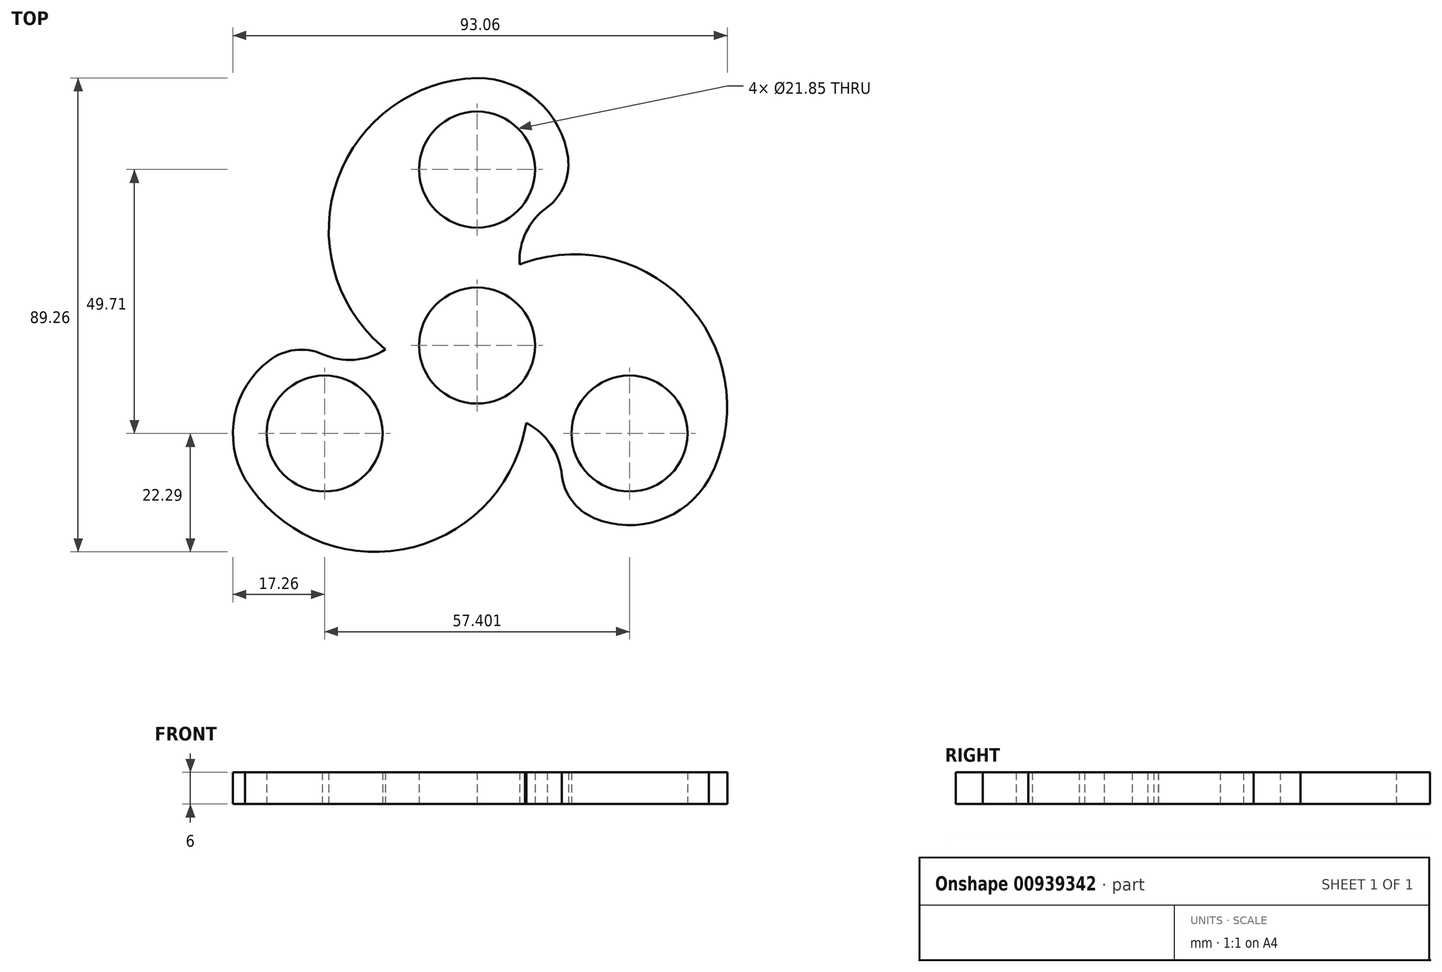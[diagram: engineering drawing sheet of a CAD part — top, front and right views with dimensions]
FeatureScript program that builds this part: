
annotation { "Feature Type Name" : "Feature", "Feature Type Description" : "" }
export const myFeature = defineFeature(function(context is Context, id is Id, definition is map)
    precondition{}
    {
        {
            var Q0;
            Q0=qCreatedBy(makeId("Top.planeOp"),FACE);
            var sketch = newSketch(context, id + "F0", { "sketchPlane" : qUnion([Q0])});
            skCircle(sketch, "E0", {"center": v(0, 0) * mm, "radius": 277.5 * mm});
            skCircle(sketch, "E1", {"center": v(0, 0) * mm, "radius": 266.7 * mm});
            skCircle(sketch, "E2", {"center": v(0, 0) * mm, "radius": 10.93 * mm});
            skCircle(sketch, "E3", {"center": v(0, 33.14) * mm, "radius": 10.93 * mm});
            skArc(sketch, "E4", {"start": v(17.13, 35.3) * mm, "mid": v(11.42, 46.09) * mm, "end": v(0, 50.4) * mm});
            skPoint(sketch, "E5.visualSharp", {"position": v(16.45, 27.92) * mm});
            skArc(sketch, "E5.filletArc", {"start": v(13.2, 26.04) * mm, "mid": v(16.4, 30.14) * mm, "end": v(17.13, 35.3) * mm});
            skCircle(sketch, "E6.1.2", {"center": v(-28.7, -16.57) * mm, "radius": 10.93 * mm});
            skCircle(sketch, "E6.2.2", {"center": v(28.7, -16.57) * mm, "radius": 10.93 * mm});
            skPoint(sketch, "E7.visualSharp", {"position": v(15.96, -24.44) * mm});
            skArc(sketch, "E7.filletArc", {"start": v(16.14, -25.52) * mm, "mid": v(15.76, -24.25) * mm, "end": v(15.21, -23.04) * mm});
            skLineSegment(sketch, "E8", {"start": v(-26.6, -2.69) * mm, "end": v(-27.22, -2.01) * mm});
            skPoint(sketch, "E9.end.orphan", {"position": v(-24.66, -2.01) * mm});
            skLineSegment(sketch, "E10", {"start": v(-29.15, -1.6) * mm, "end": v(-27.22, -2.01) * mm});
            skLineSegment(sketch, "E11", {"start": v(9.03, -15.65) * mm, "end": v(9.3, -14.61) * mm});
            skArc(sketch, "E12", {"start": v(0, 50.4) * mm, "mid": v(-26.23, 31.37) * mm, "end": v(-18.07, 0) * mm});
            skArc(sketch, "E13", {"start": v(13.2, 26.04) * mm, "mid": v(9.22, 21.33) * mm, "end": v(8, 15.3) * mm});
            skArc(sketch, "E14.1.0", {"start": v(-43.65, -25.2) * mm, "mid": v(-14.05, -38.4) * mm, "end": v(9.03, -15.65) * mm});
            skArc(sketch, "E14.1.1", {"start": v(-39.14, -2.82) * mm, "mid": v(-45.62, -13.16) * mm, "end": v(-43.65, -25.2) * mm});
            skArc(sketch, "E14.1.2", {"start": v(-29.15, -1.6) * mm, "mid": v(-23.08, -2.68) * mm, "end": v(-17.25, -0.71) * mm});
            skArc(sketch, "E14.1.3", {"start": v(-29.15, -1.6) * mm, "mid": v(-34.3, -0.86) * mm, "end": v(-39.14, -2.82) * mm});
            skArc(sketch, "E14.2.0", {"start": v(43.65, -25.2) * mm, "mid": v(40.28, 7.04) * mm, "end": v(9.03, 15.65) * mm});
            skArc(sketch, "E14.2.1", {"start": v(22, -32.48) * mm, "mid": v(34.2, -32.93) * mm, "end": v(43.65, -25.2) * mm});
            skArc(sketch, "E14.2.2", {"start": v(15.96, -24.44) * mm, "mid": v(13.88, -18.67) * mm, "end": v(9.3, -14.61) * mm});
            skArc(sketch, "E14.2.3", {"start": v(15.96, -24.44) * mm, "mid": v(17.9, -29.28) * mm, "end": v(22, -32.48) * mm});
            skPoint(sketch, "E15.start.orphan", {"position": v(16.71, 0) * mm});
            skLineSegment(sketch, "E16", {"start": v(9.03, 15.65) * mm, "end": v(8, 15.3) * mm});
            skLineSegment(sketch, "E17", {"start": v(-18.07, 0) * mm, "end": v(-17.25, -0.71) * mm});
            skPoint(sketch, "E18.orphan", {"position": v(-15.03, 1.14) * mm});
            skPoint(sketch, "E19.orphan", {"position": v(6.52, -13.58) * mm});
            skPoint(sketch, "E20.orphan", {"position": v(8.5, 12.44) * mm});
            skSolve(sketch);
        }
        {
            var Q0;
            Q0=makeQuery(id+"F0.imprint","IMPRINT",FACE,{"disambiguationData":[TD([[makeQuery(id+"F0.imprint","IMPRINT",EDGE,{"derivedFrom":sQuery(id+"F0.wireOp",EDGE,"E2")}),-1.0]])]});
            extrude(context, id + "F1", {"entities" : qUnion([Q0]), "depth" : 6 * mm, "offsetDistance" : 25 * mm});
        }
    });
